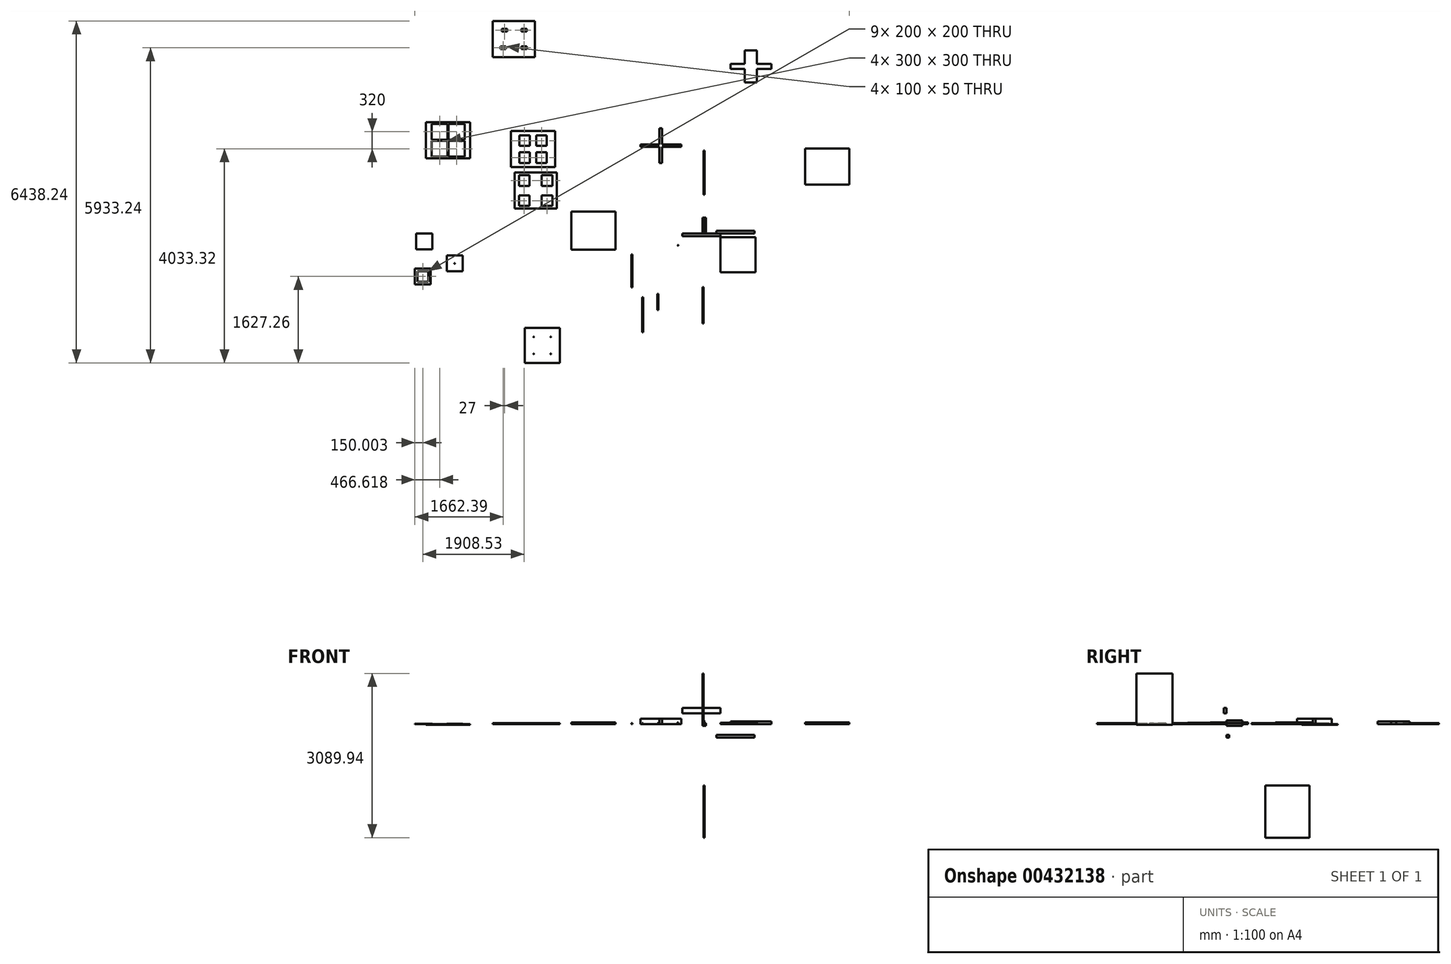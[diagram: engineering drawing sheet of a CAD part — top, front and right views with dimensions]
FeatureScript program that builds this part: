
annotation { "Feature Type Name" : "Feature", "Feature Type Description" : "" }
export const myFeature = defineFeature(function(context is Context, id is Id, definition is map)
    precondition{}
    {
        {
            var Q0;
            Q0=qCreatedBy(makeId("Front.planeOp"),FACE);
            var sketch = newSketch(context, id + "F0", { "sketchPlane" : qUnion([Q0])});
            skLineSegment(sketch, "E0.bottom", {"start": v(-15.14, 68.11) * mm, "end": v(14.86, 68.11) * mm});
            skLineSegment(sketch, "E0.top", {"start": v(-15.14, -31.89) * mm, "end": v(14.86, -31.89) * mm});
            skLineSegment(sketch, "E0.left", {"start": v(-15.14, 68.11) * mm, "end": v(-15.14, -31.89) * mm});
            skLineSegment(sketch, "E0.right", {"start": v(14.86, 68.11) * mm, "end": v(14.86, -31.89) * mm});
            skLineSegment(sketch, "E1.bottom", {"start": v(14.86, -31.89) * mm, "end": v(44.9, -31.89) * mm});
            skLineSegment(sketch, "E1.top", {"start": v(14.86, 18.11) * mm, "end": v(44.9, 18.11) * mm});
            skLineSegment(sketch, "E1.left", {"start": v(14.86, -31.89) * mm, "end": v(14.86, 18.11) * mm});
            skLineSegment(sketch, "E1.right", {"start": v(44.9, -31.89) * mm, "end": v(44.9, 18.11) * mm});
            skSolve(sketch);
        }
        {
            var Q0;
            {var subQ0=sQuery(id+"F0.wireOp",EDGE,"E1.bottom");var subQ6=sQuery(id+"F0.wireOp",EDGE,"E0.bottom");Q0=qUnion([makeQuery(id+"F0.imprint","IMPRINT",FACE,{"disambiguationData":[TD([[makeQuery(id+"F0.imprint","IMPRINT",EDGE,{"derivedFrom":subQ6}),-1.0]])]}),makeQuery(id+"F0.imprint","IMPRINT",FACE,{"disambiguationData":[TD([[makeQuery(id+"F0.imprint","IMPRINT",EDGE,{"derivedFrom":subQ0}),1.0]])]})]);}
            extrude(context, id + "F1", {"entities" : qUnion([Q0]), "oppositeDirection" : true, "depth" : 300 * mm});
        }
        {
            var Q0;
            Q0=qCreatedBy(makeId("Front.planeOp"),FACE);
            var sketch = newSketch(context, id + "F2", { "sketchPlane" : qUnion([Q0])});
            skLineSegment(sketch, "E2.bottom", {"start": v(-400.18, 302.75) * mm, "end": v(319.82, 302.75) * mm});
            skLineSegment(sketch, "E2.top", {"start": v(-400.18, 202.75) * mm, "end": v(319.82, 202.75) * mm});
            skLineSegment(sketch, "E2.left", {"start": v(-400.18, 302.75) * mm, "end": v(-400.18, 202.75) * mm});
            skLineSegment(sketch, "E2.right", {"start": v(319.82, 302.75) * mm, "end": v(319.82, 202.75) * mm});
            skSolve(sketch);
        }
        {
            var Q0;
            Q0=makeQuery(id+"F2.imprint","IMPRINT",FACE,{"disambiguationData":[TD([[makeQuery(id+"F2.imprint","IMPRINT",EDGE,{"derivedFrom":sQuery(id+"F2.wireOp",EDGE,"E2.bottom")}),-1.0]])]});
            extrude(context, id + "F3", {"entities" : qUnion([Q0]), "operationType" : NewBodyOperationType.ADD, "depth" : 50 * mm});
        }
        {
            var Q0;
            Q0=qCreatedBy(makeId("Front.planeOp"),FACE);
            var sketch = newSketch(context, id + "F4", { "sketchPlane" : qUnion([Q0])});
            skLineSegment(sketch, "E3.bottom", {"start": v(241, -207.62) * mm, "end": v(961, -207.62) * mm});
            skLineSegment(sketch, "E3.top", {"start": v(241, -257.62) * mm, "end": v(961, -257.62) * mm});
            skLineSegment(sketch, "E3.left", {"start": v(241, -207.62) * mm, "end": v(241, -257.62) * mm});
            skLineSegment(sketch, "E3.right", {"start": v(961, -207.62) * mm, "end": v(961, -257.62) * mm});
            skSolve(sketch);
        }
        {
            var Q0;
            Q0 = qSketchRegion(id + "F4", true);
            extrude(context, id + "F5", {"entities" : qUnion([Q0]), "oppositeDirection" : true, "depth" : 50 * mm});
        }
        {
            var Q0;
            Q0=qCreatedBy(makeId("Top.planeOp"),FACE);
            var sketch = newSketch(context, id + "F6", { "sketchPlane" : qUnion([Q0])});
            skLineSegment(sketch, "E4.bottom", {"start": v(-827.4, 1978.5) * mm, "end": v(-777.4, 1978.5) * mm});
            skLineSegment(sketch, "E4.top", {"start": v(-827.4, 1328.5) * mm, "end": v(-777.4, 1328.5) * mm});
            skLineSegment(sketch, "E4.left", {"start": v(-827.4, 1978.5) * mm, "end": v(-827.4, 1328.5) * mm});
            skLineSegment(sketch, "E4.right", {"start": v(-777.4, 1978.5) * mm, "end": v(-777.4, 1328.5) * mm});
            skLineSegment(sketch, "E5.bottom", {"start": v(-777.4, 1678.5) * mm, "end": v(-417.4, 1678.5) * mm});
            skLineSegment(sketch, "E5.top", {"start": v(-777.4, 1628.5) * mm, "end": v(-417.4, 1628.5) * mm});
            skLineSegment(sketch, "E5.left", {"start": v(-777.4, 1678.5) * mm, "end": v(-777.4, 1628.5) * mm});
            skLineSegment(sketch, "E5.right", {"start": v(-417.4, 1678.5) * mm, "end": v(-417.4, 1628.5) * mm});
            skLineSegment(sketch, "E6.left", {"start": v(-827.4, 1703.5) * mm, "end": v(-827.4, 1666.69) * mm});
            skLineSegment(sketch, "E7.bottom", {"start": v(-777.4, 1628.5) * mm, "end": v(-1187.4, 1628.5) * mm});
            skLineSegment(sketch, "E7.top", {"start": v(-777.4, 1678.5) * mm, "end": v(-1187.4, 1678.5) * mm});
            skLineSegment(sketch, "E7.left", {"start": v(-777.4, 1628.5) * mm, "end": v(-777.4, 1678.5) * mm});
            skLineSegment(sketch, "E7.right", {"start": v(-1187.4, 1628.5) * mm, "end": v(-1187.4, 1678.5) * mm});
            skSolve(sketch);
        }
        {
            var Q0;
            Q0 = qSketchRegion(id + "F6", true);
            extrude(context, id + "F7", {"entities" : qUnion([Q0]), "depth" : 100 * mm});
        }
        {
            var Q0;
            Q0=qCreatedBy(makeId("Right.planeOp"),FACE);
            var sketch = newSketch(context, id + "F8", { "sketchPlane" : qUnion([Q0])});
            skLineSegment(sketch, "E8.bottom", {"start": v(-1693.52, 949.93) * mm, "end": v(-1013.52, 949.93) * mm});
            skLineSegment(sketch, "E8.top", {"start": v(-1693.52, -14.07) * mm, "end": v(-1013.52, -14.07) * mm});
            skLineSegment(sketch, "E8.left", {"start": v(-1693.52, 949.93) * mm, "end": v(-1693.52, -14.07) * mm});
            skLineSegment(sketch, "E8.right", {"start": v(-1013.52, 949.93) * mm, "end": v(-1013.52, -14.07) * mm});
            skSolve(sketch);
        }
        {
            var Q0;
            Q0=makeQuery(id+"F8.imprint","IMPRINT",FACE,{"disambiguationData":[TD([[makeQuery(id+"F8.imprint","IMPRINT",EDGE,{"derivedFrom":sQuery(id+"F8.wireOp",EDGE,"E8.bottom")}),-1.0]])]});
            extrude(context, id + "F9", {"entities" : qUnion([Q0]), "oppositeDirection" : true, "depth" : 18 * mm, "offsetDistance" : 25 * mm});
        }
        {
            var Q0;
            Q0=qCreatedBy(makeId("Top.planeOp"),FACE);
            var sketch = newSketch(context, id + "F10", { "sketchPlane" : qUnion([Q0])});
            skLineSegment(sketch, "E9.bottom", {"start": v(1912.98, 1600.6) * mm, "end": v(2742.98, 1600.6) * mm});
            skLineSegment(sketch, "E9.top", {"start": v(1912.98, 920.6) * mm, "end": v(2742.98, 920.6) * mm});
            skLineSegment(sketch, "E9.left", {"start": v(1912.98, 1600.6) * mm, "end": v(1912.98, 920.6) * mm});
            skLineSegment(sketch, "E9.right", {"start": v(2742.98, 1600.6) * mm, "end": v(2742.98, 920.6) * mm});
            skSolve(sketch);
        }
        {
            var Q0;
            Q0=makeQuery(id+"F10.imprint","IMPRINT",FACE,{"disambiguationData":[TD([[makeQuery(id+"F10.imprint","IMPRINT",EDGE,{"derivedFrom":sQuery(id+"F10.wireOp",EDGE,"E9.bottom")}),-1.0]])]});
            extrude(context, id + "F11", {"entities" : qUnion([Q0]), "depth" : 30 * mm});
        }
        {
            var Q0;
            Q0=qCreatedBy(makeId("Right.planeOp"),FACE);
            var sketch = newSketch(context, id + "F12", { "sketchPlane" : qUnion([Q0])});
            skLineSegment(sketch, "E10.bottom", {"start": v(731.74, -1158.01) * mm, "end": v(1561.74, -1158.01) * mm});
            skLineSegment(sketch, "E10.top", {"start": v(731.74, -2140.01) * mm, "end": v(1561.74, -2140.01) * mm});
            skLineSegment(sketch, "E10.left", {"start": v(731.74, -1158.01) * mm, "end": v(731.74, -2140.01) * mm});
            skLineSegment(sketch, "E10.right", {"start": v(1561.74, -1158.01) * mm, "end": v(1561.74, -2140.01) * mm});
            skSolve(sketch);
        }
        {
            var Q0;
            Q0 = qSketchRegion(id + "F12", true);
            extrude(context, id + "F13", {"entities" : qUnion([Q0]), "depth" : 18 * mm, "offsetDistance" : 25 * mm});
        }
        {
            var Q0;
            Q0=qCreatedBy(makeId("Top.planeOp"),FACE);
            var sketch = newSketch(context, id + "F14", { "sketchPlane" : qUnion([Q0])});
            skLineSegment(sketch, "E11.bottom", {"start": v(-2488.25, 409.31) * mm, "end": v(-1658.25, 409.31) * mm});
            skLineSegment(sketch, "E11.top", {"start": v(-2488.25, -306.69) * mm, "end": v(-1658.25, -306.69) * mm});
            skLineSegment(sketch, "E11.left", {"start": v(-2488.25, 409.31) * mm, "end": v(-2488.25, -306.69) * mm});
            skLineSegment(sketch, "E11.right", {"start": v(-1658.25, 409.31) * mm, "end": v(-1658.25, -306.69) * mm});
            skSolve(sketch);
        }
        {
            var Q0;
            Q0=makeQuery(id+"F14.imprint","IMPRINT",FACE,{"disambiguationData":[TD([[makeQuery(id+"F14.imprint","IMPRINT",EDGE,{"derivedFrom":sQuery(id+"F14.wireOp",EDGE,"E11.bottom")}),-1.0]])]});
            extrude(context, id + "F15", {"entities" : qUnion([Q0]), "depth" : 30 * mm});
        }
        {
            var Q0;
            Q0=qCreatedBy(makeId("Top.planeOp"),FACE);
            var sketch = newSketch(context, id + "F16", { "sketchPlane" : qUnion([Q0])});
            skLineSegment(sketch, "E12.bottom", {"start": v(1006.96, 3446.43) * mm, "end": v(776.96, 3446.43) * mm});
            skLineSegment(sketch, "E12.top", {"start": v(1006.96, 2846.43) * mm, "end": v(776.96, 2846.43) * mm});
            skLineSegment(sketch, "E12.left", {"start": v(1006.96, 3446.43) * mm, "end": v(1006.96, 2846.43) * mm});
            skLineSegment(sketch, "E12.right", {"start": v(776.96, 3446.43) * mm, "end": v(776.96, 2846.43) * mm});
            skLineSegment(sketch, "E13.bottom", {"start": v(1006.96, 3196.43) * mm, "end": v(1276.96, 3196.43) * mm});
            skLineSegment(sketch, "E13.top", {"start": v(1006.96, 3096.43) * mm, "end": v(1276.96, 3096.43) * mm});
            skLineSegment(sketch, "E13.left", {"start": v(1006.96, 3196.43) * mm, "end": v(1006.96, 3096.43) * mm});
            skLineSegment(sketch, "E13.right", {"start": v(1276.96, 3196.43) * mm, "end": v(1276.96, 3096.43) * mm});
            skPoint(sketch, "E14.firstSnap0", {"position": v(1141.96, 3096.43) * mm});
            skLineSegment(sketch, "E14.bottom", {"start": v(776.96, 3096.43) * mm, "end": v(506.96, 3096.43) * mm});
            skLineSegment(sketch, "E14.top", {"start": v(776.96, 3196.43) * mm, "end": v(506.96, 3196.43) * mm});
            skLineSegment(sketch, "E14.left", {"start": v(776.96, 3096.43) * mm, "end": v(776.96, 3196.43) * mm});
            skLineSegment(sketch, "E14.right", {"start": v(506.96, 3096.43) * mm, "end": v(506.96, 3196.43) * mm});
            skSolve(sketch);
        }
        {
            var Q0;
            {var subQ2=sQuery(id+"F16.wireOp",EDGE,"E13.bottom");Q0=makeQuery(id+"F16.imprint","IMPRINT",FACE,{"disambiguationData":[TD([[makeQuery(id+"F16.imprint","IMPRINT",EDGE,{"derivedFrom":subQ2}),-1.0]])]});}
            var Q1;
            {var subQ0=sQuery(id+"F16.wireOp",EDGE,"E14.bottom");Q1=makeQuery(id+"F16.imprint","IMPRINT",FACE,{"disambiguationData":[TD([[makeQuery(id+"F16.imprint","IMPRINT",EDGE,{"derivedFrom":subQ0}),-1.0]])]});}
            var Q2;
            {var subQ1=sQuery(id+"F16.wireOp",EDGE,"E12.bottom");Q2=makeQuery(id+"F16.imprint","IMPRINT",FACE,{"disambiguationData":[TD([[makeQuery(id+"F16.imprint","IMPRINT",EDGE,{"derivedFrom":subQ1}),1.0]])]});}
            extrude(context, id + "F17", {"entities" : qUnion([Q0, Q1, Q2]), "depth" : 50 * mm});
        }
        {
            var Q0;
            Q0=qCreatedBy(makeId("Top.planeOp"),FACE);
            var sketch = newSketch(context, id + "F18", { "sketchPlane" : qUnion([Q0])});
            skLineSegment(sketch, "E15.bottom", {"start": v(-3622.9, 1928.44) * mm, "end": v(-2792.9, 1928.44) * mm});
            skLineSegment(sketch, "E15.top", {"start": v(-3622.9, 1248.44) * mm, "end": v(-2792.9, 1248.44) * mm});
            skLineSegment(sketch, "E15.left", {"start": v(-3622.9, 1928.44) * mm, "end": v(-3622.9, 1248.44) * mm});
            skLineSegment(sketch, "E15.right", {"start": v(-2792.9, 1928.44) * mm, "end": v(-2792.9, 1248.44) * mm});
            skLineSegment(sketch, "E16.bottom", {"start": v(-3467.9, 1328.44) * mm, "end": v(-3267.9, 1328.44) * mm});
            skLineSegment(sketch, "E16.top", {"start": v(-3467.9, 1528.44) * mm, "end": v(-3267.9, 1528.44) * mm});
            skLineSegment(sketch, "E16.left", {"start": v(-3467.9, 1328.44) * mm, "end": v(-3467.9, 1528.44) * mm});
            skLineSegment(sketch, "E16.right", {"start": v(-3267.9, 1328.44) * mm, "end": v(-3267.9, 1528.44) * mm});
            skLineSegment(sketch, "E17.bottom", {"start": v(-3147.9, 1328.44) * mm, "end": v(-2947.9, 1328.44) * mm});
            skLineSegment(sketch, "E17.top", {"start": v(-3147.9, 1528.44) * mm, "end": v(-2947.9, 1528.44) * mm});
            skLineSegment(sketch, "E17.left", {"start": v(-3147.9, 1328.44) * mm, "end": v(-3147.9, 1528.44) * mm});
            skLineSegment(sketch, "E17.right", {"start": v(-2947.9, 1328.44) * mm, "end": v(-2947.9, 1528.44) * mm});
            skLineSegment(sketch, "E18.bottom", {"start": v(-3467.9, 1848.44) * mm, "end": v(-3267.9, 1848.44) * mm});
            skLineSegment(sketch, "E18.top", {"start": v(-3467.9, 1648.44) * mm, "end": v(-3267.9, 1648.44) * mm});
            skLineSegment(sketch, "E18.left", {"start": v(-3467.9, 1848.44) * mm, "end": v(-3467.9, 1648.44) * mm});
            skLineSegment(sketch, "E18.right", {"start": v(-3267.9, 1848.44) * mm, "end": v(-3267.9, 1648.44) * mm});
            skLineSegment(sketch, "E19.bottom", {"start": v(-3147.9, 1848.44) * mm, "end": v(-2947.9, 1848.44) * mm});
            skLineSegment(sketch, "E19.top", {"start": v(-3147.9, 1648.44) * mm, "end": v(-2947.9, 1648.44) * mm});
            skLineSegment(sketch, "E19.left", {"start": v(-3147.9, 1848.44) * mm, "end": v(-3147.9, 1648.44) * mm});
            skLineSegment(sketch, "E19.right", {"start": v(-2947.9, 1848.44) * mm, "end": v(-2947.9, 1648.44) * mm});
            skSolve(sketch);
        }
        {
            var Q0;
            Q0=qCreatedBy(makeId("Top.planeOp"),FACE);
            var sketch = newSketch(context, id + "F19", { "sketchPlane" : qUnion([Q0])});
            skLineSegment(sketch, "E20.bottom", {"start": v(-5220.72, 2095.79) * mm, "end": v(-4390.72, 2095.79) * mm});
            skLineSegment(sketch, "E20.top", {"start": v(-5220.72, 1415.79) * mm, "end": v(-4390.72, 1415.79) * mm});
            skLineSegment(sketch, "E20.left", {"start": v(-5220.72, 2095.79) * mm, "end": v(-5220.72, 1415.79) * mm});
            skLineSegment(sketch, "E20.right", {"start": v(-4390.72, 2095.79) * mm, "end": v(-4390.72, 1415.79) * mm});
            skLineSegment(sketch, "E21.bottom", {"start": v(-4470.72, 1415.79) * mm, "end": v(-4770.72, 1415.79) * mm});
            skLineSegment(sketch, "E22.bottom", {"start": v(-5115.72, 1745.79) * mm, "end": v(-4815.72, 1745.79) * mm});
            skLineSegment(sketch, "E22.top", {"start": v(-5115.72, 1445.79) * mm, "end": v(-4815.72, 1445.79) * mm});
            skLineSegment(sketch, "E22.left", {"start": v(-5115.72, 1745.79) * mm, "end": v(-5115.72, 1445.79) * mm});
            skLineSegment(sketch, "E22.right", {"start": v(-4815.72, 1745.79) * mm, "end": v(-4815.72, 1445.79) * mm});
            skLineSegment(sketch, "E23.bottom", {"start": v(-5115.72, 2065.79) * mm, "end": v(-4815.72, 2065.79) * mm});
            skLineSegment(sketch, "E23.top", {"start": v(-5115.72, 1765.79) * mm, "end": v(-4815.72, 1765.79) * mm});
            skLineSegment(sketch, "E23.left", {"start": v(-5115.72, 2065.79) * mm, "end": v(-5115.72, 1765.79) * mm});
            skLineSegment(sketch, "E23.right", {"start": v(-4815.72, 2065.79) * mm, "end": v(-4815.72, 1765.79) * mm});
            skLineSegment(sketch, "E24.bottom", {"start": v(-4795.72, 2065.79) * mm, "end": v(-4495.72, 2065.79) * mm});
            skLineSegment(sketch, "E24.top", {"start": v(-4795.72, 1765.79) * mm, "end": v(-4495.72, 1765.79) * mm});
            skLineSegment(sketch, "E24.left", {"start": v(-4795.72, 2065.79) * mm, "end": v(-4795.72, 1765.79) * mm});
            skLineSegment(sketch, "E24.right", {"start": v(-4495.72, 2065.79) * mm, "end": v(-4495.72, 1765.79) * mm});
            skLineSegment(sketch, "E25.bottom", {"start": v(-4795.72, 1745.79) * mm, "end": v(-4495.72, 1745.79) * mm});
            skLineSegment(sketch, "E25.top", {"start": v(-4795.72, 1445.79) * mm, "end": v(-4495.72, 1445.79) * mm});
            skLineSegment(sketch, "E25.left", {"start": v(-4795.72, 1745.79) * mm, "end": v(-4795.72, 1445.79) * mm});
            skLineSegment(sketch, "E25.right", {"start": v(-4495.72, 1745.79) * mm, "end": v(-4495.72, 1445.79) * mm});
            skSolve(sketch);
        }
        {
            var Q0;
            {var subQ2=sQuery(id+"F19.wireOp",EDGE,"E20.left");Q0=makeQuery(id+"F19.imprint","IMPRINT",FACE,{"disambiguationData":[TD([[makeQuery(id+"F19.imprint","IMPRINT",EDGE,{"derivedFrom":subQ2}),1.0]])]});}
            extrude(context, id + "F20", {"entities" : qUnion([Q0]), "oppositeDirection" : true, "depth" : 18 * mm, "offsetDistance" : 25 * mm});
        }
        {
            var Q0;
            Q0=qCreatedBy(makeId("Top.planeOp"),FACE);
            var sketch = newSketch(context, id + "F21", { "sketchPlane" : qUnion([Q0])});
            skLineSegment(sketch, "E26.bottom", {"start": v(-5406.31, -0.83) * mm, "end": v(-5106.31, -0.83) * mm});
            skLineSegment(sketch, "E26.top", {"start": v(-5406.31, -300.83) * mm, "end": v(-5106.31, -300.83) * mm});
            skLineSegment(sketch, "E26.left", {"start": v(-5406.31, -0.83) * mm, "end": v(-5406.31, -300.83) * mm});
            skLineSegment(sketch, "E26.right", {"start": v(-5106.31, -0.83) * mm, "end": v(-5106.31, -300.83) * mm});
            skSolve(sketch);
        }
        {
            var Q0;
            Q0=makeQuery(id+"F21.imprint","IMPRINT",FACE,{"disambiguationData":[TD([[makeQuery(id+"F21.imprint","IMPRINT",EDGE,{"derivedFrom":sQuery(id+"F21.wireOp",EDGE,"E26.bottom")}),-1.0]])]});
            extrude(context, id + "F22", {"entities" : qUnion([Q0]), "depth" : 2 * mm, "offsetDistance" : 25 * mm});
        }
        {
            var Q0;
            Q0=qCreatedBy(makeId("Top.planeOp"),FACE);
            var sketch = newSketch(context, id + "F23", { "sketchPlane" : qUnion([Q0])});
            skLineSegment(sketch, "E27.bottom", {"start": v(-5432.34, -660.27) * mm, "end": v(-5132.34, -660.27) * mm});
            skLineSegment(sketch, "E27.top", {"start": v(-5432.34, -960.27) * mm, "end": v(-5132.34, -960.27) * mm});
            skLineSegment(sketch, "E27.left", {"start": v(-5432.34, -660.27) * mm, "end": v(-5432.34, -960.27) * mm});
            skLineSegment(sketch, "E27.right", {"start": v(-5132.34, -660.27) * mm, "end": v(-5132.34, -960.27) * mm});
            skLineSegment(sketch, "E28.bottom", {"start": v(-5382.34, -710.27) * mm, "end": v(-5182.34, -710.27) * mm});
            skLineSegment(sketch, "E28.top", {"start": v(-5382.34, -910.27) * mm, "end": v(-5182.34, -910.27) * mm});
            skLineSegment(sketch, "E28.left", {"start": v(-5382.34, -710.27) * mm, "end": v(-5382.34, -910.27) * mm});
            skLineSegment(sketch, "E28.right", {"start": v(-5182.34, -710.27) * mm, "end": v(-5182.34, -910.27) * mm});
            skSolve(sketch);
        }
        {
            var Q0;
            Q0=makeQuery(id+"F23.imprint","IMPRINT",FACE,{"disambiguationData":[TD([[makeQuery(id+"F23.imprint","IMPRINT",EDGE,{"derivedFrom":sQuery(id+"F23.wireOp",EDGE,"E27.bottom")}),-1.0]])]});
            extrude(context, id + "F24", {"entities" : qUnion([Q0]), "depth" : 2 * mm, "offsetDistance" : 25 * mm});
        }
        {
            var Q0;
            Q0=qCreatedBy(makeId("Top.planeOp"),FACE);
            var sketch = newSketch(context, id + "F25", { "sketchPlane" : qUnion([Q0])});
            skLineSegment(sketch, "E29.bottom", {"start": v(-4832.48, -413.53) * mm, "end": v(-4532.48, -413.53) * mm});
            skLineSegment(sketch, "E29.top", {"start": v(-4832.48, -713.53) * mm, "end": v(-4532.48, -713.53) * mm});
            skLineSegment(sketch, "E29.left", {"start": v(-4832.48, -413.53) * mm, "end": v(-4832.48, -713.53) * mm});
            skLineSegment(sketch, "E29.right", {"start": v(-4532.48, -413.53) * mm, "end": v(-4532.48, -713.53) * mm});
            skCircle(sketch, "E30", {"center": v(-4682.48, -563.53) * mm, "radius": 6 * mm});
            skSolve(sketch);
        }
        {
            var Q0;
            Q0=makeQuery(id+"F25.imprint","IMPRINT",FACE,{"disambiguationData":[TD([[makeQuery(id+"F25.imprint","IMPRINT",EDGE,{"derivedFrom":sQuery(id+"F25.wireOp",EDGE,"E29.bottom")}),-1.0]])]});
            extrude(context, id + "F26", {"entities" : qUnion([Q0]), "depth" : 5 * mm, "offsetDistance" : 25 * mm});
        }
        {
            var Q0;
            Q0=qCreatedBy(makeId("Top.planeOp"),FACE);
            var sketch = newSketch(context, id + "F27", { "sketchPlane" : qUnion([Q0])});
            skLineSegment(sketch, "E31.bottom", {"start": v(-3555.8, 1147.58) * mm, "end": v(-2761.8, 1147.58) * mm});
            skLineSegment(sketch, "E31.top", {"start": v(-3555.8, 467.58) * mm, "end": v(-2761.8, 467.58) * mm});
            skLineSegment(sketch, "E31.left", {"start": v(-3555.8, 1147.58) * mm, "end": v(-3555.8, 467.58) * mm});
            skLineSegment(sketch, "E31.right", {"start": v(-2761.8, 1147.58) * mm, "end": v(-2761.8, 467.58) * mm});
            skLineSegment(sketch, "E32.bottom", {"start": v(-3473.8, 1097.58) * mm, "end": v(-3273.8, 1097.58) * mm});
            skLineSegment(sketch, "E32.top", {"start": v(-3473.8, 897.58) * mm, "end": v(-3273.8, 897.58) * mm});
            skLineSegment(sketch, "E32.left", {"start": v(-3473.8, 1097.58) * mm, "end": v(-3473.8, 897.58) * mm});
            skLineSegment(sketch, "E32.right", {"start": v(-3273.8, 1097.58) * mm, "end": v(-3273.8, 897.58) * mm});
            skLineSegment(sketch, "E33.bottom", {"start": v(-3473.8, 717.58) * mm, "end": v(-3273.8, 717.58) * mm});
            skLineSegment(sketch, "E33.top", {"start": v(-3473.8, 517.58) * mm, "end": v(-3273.8, 517.58) * mm});
            skLineSegment(sketch, "E33.left", {"start": v(-3473.8, 717.58) * mm, "end": v(-3473.8, 517.58) * mm});
            skLineSegment(sketch, "E33.right", {"start": v(-3273.8, 717.58) * mm, "end": v(-3273.8, 517.58) * mm});
            skLineSegment(sketch, "E34.bottom", {"start": v(-3043.8, 1097.58) * mm, "end": v(-2843.8, 1097.58) * mm});
            skLineSegment(sketch, "E34.top", {"start": v(-3043.8, 897.58) * mm, "end": v(-2843.8, 897.58) * mm});
            skLineSegment(sketch, "E34.left", {"start": v(-3043.8, 1097.58) * mm, "end": v(-3043.8, 897.58) * mm});
            skLineSegment(sketch, "E34.right", {"start": v(-2843.8, 1097.58) * mm, "end": v(-2843.8, 897.58) * mm});
            skLineSegment(sketch, "E35.bottom", {"start": v(-3043.8, 717.58) * mm, "end": v(-2843.8, 717.58) * mm});
            skLineSegment(sketch, "E35.top", {"start": v(-3043.8, 517.58) * mm, "end": v(-2843.8, 517.58) * mm});
            skLineSegment(sketch, "E35.left", {"start": v(-3043.8, 717.58) * mm, "end": v(-3043.8, 517.58) * mm});
            skLineSegment(sketch, "E35.right", {"start": v(-2843.8, 717.58) * mm, "end": v(-2843.8, 517.58) * mm});
            skSolve(sketch);
        }
        {
            var Q0;
            Q0 = qSketchRegion(id + "F27", true);
            extrude(context, id + "F28", {"entities" : qUnion([Q0]), "depth" : 18 * mm});
        }
        {
            var Q0;
            Q0=qCreatedBy(makeId("Top.planeOp"),FACE);
            var sketch = newSketch(context, id + "F29", { "sketchPlane" : qUnion([Q0])});
            skLineSegment(sketch, "E36.bottom", {"start": v(-3969.95, 4000.71) * mm, "end": v(-3175.95, 4000.71) * mm});
            skLineSegment(sketch, "E36.top", {"start": v(-3969.95, 3320.71) * mm, "end": v(-3175.95, 3320.71) * mm});
            skLineSegment(sketch, "E36.left", {"start": v(-3969.95, 4000.71) * mm, "end": v(-3969.95, 3320.71) * mm});
            skLineSegment(sketch, "E36.right", {"start": v(-3175.95, 4000.71) * mm, "end": v(-3175.95, 3320.71) * mm});
            skLineSegment(sketch, "E37.bottom", {"start": v(-3792.95, 3850.71) * mm, "end": v(-3692.95, 3850.71) * mm});
            skLineSegment(sketch, "E37.top", {"start": v(-3792.95, 3800.71) * mm, "end": v(-3692.95, 3800.71) * mm});
            skLineSegment(sketch, "E37.left", {"start": v(-3792.95, 3850.71) * mm, "end": v(-3792.95, 3800.71) * mm});
            skLineSegment(sketch, "E37.right", {"start": v(-3692.95, 3850.71) * mm, "end": v(-3692.95, 3800.71) * mm});
            skLineSegment(sketch, "E38.bottom", {"start": v(-3425.95, 3850.71) * mm, "end": v(-3325.95, 3850.71) * mm});
            skLineSegment(sketch, "E38.top", {"start": v(-3425.95, 3800.71) * mm, "end": v(-3325.95, 3800.71) * mm});
            skLineSegment(sketch, "E38.left", {"start": v(-3425.95, 3850.71) * mm, "end": v(-3425.95, 3800.71) * mm});
            skLineSegment(sketch, "E38.right", {"start": v(-3325.95, 3850.71) * mm, "end": v(-3325.95, 3800.71) * mm});
            skLineSegment(sketch, "E39.bottom", {"start": v(-3819.95, 3520.71) * mm, "end": v(-3719.95, 3520.71) * mm});
            skLineSegment(sketch, "E39.top", {"start": v(-3819.95, 3470.71) * mm, "end": v(-3719.95, 3470.71) * mm});
            skLineSegment(sketch, "E39.left", {"start": v(-3819.95, 3520.71) * mm, "end": v(-3819.95, 3470.71) * mm});
            skLineSegment(sketch, "E39.right", {"start": v(-3719.95, 3520.71) * mm, "end": v(-3719.95, 3470.71) * mm});
            skLineSegment(sketch, "E40.bottom", {"start": v(-3425.95, 3520.71) * mm, "end": v(-3325.95, 3520.71) * mm});
            skLineSegment(sketch, "E40.top", {"start": v(-3425.95, 3470.71) * mm, "end": v(-3325.95, 3470.71) * mm});
            skLineSegment(sketch, "E40.left", {"start": v(-3425.95, 3520.71) * mm, "end": v(-3425.95, 3470.71) * mm});
            skLineSegment(sketch, "E40.right", {"start": v(-3325.95, 3520.71) * mm, "end": v(-3325.95, 3470.71) * mm});
            skSolve(sketch);
        }
        {
            var Q0;
            Q0=makeQuery(id+"F29.imprint","IMPRINT",FACE,{"disambiguationData":[TD([[makeQuery(id+"F29.imprint","IMPRINT",EDGE,{"derivedFrom":sQuery(id+"F29.wireOp",EDGE,"E36.bottom")}),-1.0]])]});
            extrude(context, id + "F30", {"entities" : qUnion([Q0]), "depth" : 18 * mm});
        }
        {
            var Q0;
            Q0 = qSketchRegion(id + "F18", true);
            extrude(context, id + "F31", {"entities" : qUnion([Q0]), "depth" : 18 * mm, "offsetDistance" : 25 * mm});
        }
        {
            var Q0;
            Q0=qCreatedBy(makeId("Top.planeOp"),FACE);
            var sketch = newSketch(context, id + "F32", { "sketchPlane" : qUnion([Q0])});
            skLineSegment(sketch, "E41.bottom", {"start": v(-1136.43, -1863.46) * mm, "end": v(-1156.43, -1863.46) * mm});
            skLineSegment(sketch, "E41.top", {"start": v(-1136.43, -1203.46) * mm, "end": v(-1156.43, -1203.46) * mm});
            skLineSegment(sketch, "E41.left", {"start": v(-1136.43, -1863.46) * mm, "end": v(-1136.43, -1203.46) * mm});
            skLineSegment(sketch, "E41.right", {"start": v(-1156.43, -1863.46) * mm, "end": v(-1156.43, -1203.46) * mm});
            skSolve(sketch);
        }
        {
            var Q0;
            Q0=makeQuery(id+"F32.imprint","IMPRINT",FACE,{"disambiguationData":[TD([[makeQuery(id+"F32.imprint","IMPRINT",EDGE,{"derivedFrom":sQuery(id+"F32.wireOp",EDGE,"E41.bottom")}),-1.0]])]});
            extrude(context, id + "F33", {"entities" : qUnion([Q0]), "depth" : 18 * mm, "offsetDistance" : 25 * mm});
        }
        {
            var Q0;
            Q0=qCreatedBy(makeId("Top.planeOp"),FACE);
            var sketch = newSketch(context, id + "F34", { "sketchPlane" : qUnion([Q0])});
            skLineSegment(sketch, "E42.bottom", {"start": v(-870.07, -1139.2) * mm, "end": v(-850.07, -1139.2) * mm});
            skLineSegment(sketch, "E42.top", {"start": v(-870.07, -1439.2) * mm, "end": v(-850.07, -1439.2) * mm});
            skLineSegment(sketch, "E42.left", {"start": v(-870.07, -1139.2) * mm, "end": v(-870.07, -1439.2) * mm});
            skLineSegment(sketch, "E42.right", {"start": v(-850.07, -1139.2) * mm, "end": v(-850.07, -1439.2) * mm});
            skSolve(sketch);
        }
        {
            var Q0;
            Q0=makeQuery(id+"F34.imprint","IMPRINT",FACE,{"disambiguationData":[TD([[makeQuery(id+"F34.imprint","IMPRINT",EDGE,{"derivedFrom":sQuery(id+"F34.wireOp",EDGE,"E42.bottom")}),-1.0]])]});
            extrude(context, id + "F35", {"entities" : qUnion([Q0]), "depth" : 18 * mm, "offsetDistance" : 25 * mm});
        }
        {
            var Q0;
            Q0=qCreatedBy(makeId("Top.planeOp"),FACE);
            var sketch = newSketch(context, id + "F36", { "sketchPlane" : qUnion([Q0])});
            skLineSegment(sketch, "E43.bottom", {"start": v(-1340.2, -395.56) * mm, "end": v(-1360.2, -395.56) * mm});
            skLineSegment(sketch, "E43.top", {"start": v(-1340.2, -1015.56) * mm, "end": v(-1360.2, -1015.56) * mm});
            skLineSegment(sketch, "E43.left", {"start": v(-1340.2, -395.56) * mm, "end": v(-1340.2, -1015.56) * mm});
            skLineSegment(sketch, "E43.right", {"start": v(-1360.2, -395.56) * mm, "end": v(-1360.2, -1015.56) * mm});
            skSolve(sketch);
        }
        {
            var Q0;
            Q0=makeQuery(id+"F36.imprint","IMPRINT",FACE,{"disambiguationData":[TD([[makeQuery(id+"F36.imprint","IMPRINT",EDGE,{"derivedFrom":sQuery(id+"F36.wireOp",EDGE,"E43.bottom")}),1.0]])]});
            extrude(context, id + "F37", {"entities" : qUnion([Q0]), "depth" : 18 * mm, "offsetDistance" : 25 * mm});
        }
        {
            var Q0;
            Q0=qCreatedBy(makeId("Top.planeOp"),FACE);
            var sketch = newSketch(context, id + "F38", { "sketchPlane" : qUnion([Q0])});
            skLineSegment(sketch, "E44.bottom", {"start": v(-3365.48, -1777.53) * mm, "end": v(-2705.48, -1777.53) * mm});
            skLineSegment(sketch, "E44.top", {"start": v(-3365.48, -2437.53) * mm, "end": v(-2705.48, -2437.53) * mm});
            skLineSegment(sketch, "E44.left", {"start": v(-3365.48, -1777.53) * mm, "end": v(-3365.48, -2437.53) * mm});
            skLineSegment(sketch, "E44.right", {"start": v(-2705.48, -1777.53) * mm, "end": v(-2705.48, -2437.53) * mm});
            skCircle(sketch, "E45", {"center": v(-3195.48, -1947.53) * mm, "radius": 6 * mm});
            skCircle(sketch, "E46", {"center": v(-2875.48, -1947.53) * mm, "radius": 6 * mm});
            skCircle(sketch, "E47", {"center": v(-3195.48, -2267.53) * mm, "radius": 6 * mm});
            skCircle(sketch, "E48", {"center": v(-2875.48, -2267.53) * mm, "radius": 6 * mm});
            skSolve(sketch);
        }
        {
            var Q0;
            Q0=makeQuery(id+"F38.imprint","IMPRINT",FACE,{"disambiguationData":[TD([[makeQuery(id+"F38.imprint","IMPRINT",EDGE,{"derivedFrom":sQuery(id+"F38.wireOp",EDGE,"E44.bottom")}),-1.0]])]});
            extrude(context, id + "F39", {"entities" : qUnion([Q0]), "depth" : 18 * mm, "offsetDistance" : 25 * mm});
        }
        {
            var Q0;
            Q0=qCreatedBy(makeId("Top.planeOp"),FACE);
            var sketch = newSketch(context, id + "F40", { "sketchPlane" : qUnion([Q0])});
            skCircle(sketch, "E49", {"center": v(-478.1, -224.35) * mm, "radius": 6 * mm});
            skSolve(sketch);
        }
        {
            var Q0;
            Q0=makeQuery(id+"F40.imprint","IMPRINT",FACE,{"disambiguationData":[TD([[makeQuery(id+"F40.imprint","IMPRINT",EDGE,{"derivedFrom":sQuery(id+"F40.wireOp",EDGE,"E49")}),1.0]])]});
            extrude(context, id + "F41", {"entities" : qUnion([Q0]), "depth" : 32 * mm, "offsetDistance" : 25 * mm});
        }
        {
            var Q0;
            Q0=sQuery(id+"F40.wireOp",VERTEX,"E49.center");
            var Q1;
            Q1=makeQuery(id+"F41.opExtrude","SWEPT_BODY",BODY,{"disambiguationData":[OSD([sQuery(id+"F40.wireOp",EDGE,"E49")])]});
            hole(context, id + "F42", {"style" : HoleStyle.SIMPLE, "endStyle" : HoleEndStyle.THROUGH, "oppositeDirection" : true, "holeDiameter" : 11 * mm, "majorDiameter" : 5 * mm, "isTappedThrough" : true, "tappedDepth" : 12 * mm, "tapClearance" : 3, "locations" : qUnion([Q0]), "scope" : qUnion([Q1])});
        }
        {
            var Q0;
            Q0=qCreatedBy(makeId("Top.planeOp"),FACE);
            var sketch = newSketch(context, id + "F43", { "sketchPlane" : qUnion([Q0])});
            skLineSegment(sketch, "E50.bottom", {"start": v(317.74, -70.23) * mm, "end": v(977.74, -70.23) * mm});
            skLineSegment(sketch, "E50.top", {"start": v(317.74, -730.23) * mm, "end": v(977.74, -730.23) * mm});
            skLineSegment(sketch, "E50.left", {"start": v(317.74, -70.23) * mm, "end": v(317.74, -730.23) * mm});
            skLineSegment(sketch, "E50.right", {"start": v(977.74, -70.23) * mm, "end": v(977.74, -730.23) * mm});
            skSolve(sketch);
        }
        {
            var Q0;
            Q0=makeQuery(id+"F43.imprint","IMPRINT",FACE,{"disambiguationData":[TD([[makeQuery(id+"F43.imprint","IMPRINT",EDGE,{"derivedFrom":sQuery(id+"F43.wireOp",EDGE,"E50.bottom")}),-1.0]])]});
            extrude(context, id + "F44", {"entities" : qUnion([Q0]), "depth" : 25 * mm, "offsetDistance" : 25 * mm});
        }
    });
